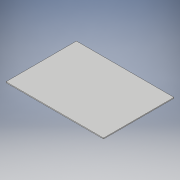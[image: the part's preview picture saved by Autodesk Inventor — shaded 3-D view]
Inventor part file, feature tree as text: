
AUTODESK INVENTOR PART (.ipt)
format: ipt  version: 2018 (Build 220112000, 112)  size: 90,112 bytes
history: native  units: in
note: dims shown in document units (in); Inventor stores cm internally (conversion verified against a paired STEP export)
features: extrude x1, sketch x1
ambient origin geometry x8: Origin, YZ Plane, XZ Plane, XY Plane, X Axis, Y Axis, Z Axis, Center Point
bodies: Solid1 (feature_tree)
feature tree (2):
  extrude  "Extrusion1"  Depth=2.5591in
  sketch  "Sketch1"  dims[d0=3.5433in d1=2.5591in d2=0.031in d3=0.0in]
